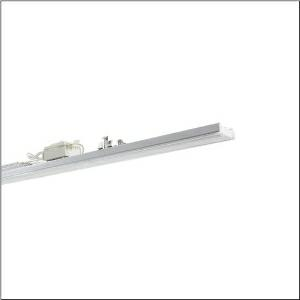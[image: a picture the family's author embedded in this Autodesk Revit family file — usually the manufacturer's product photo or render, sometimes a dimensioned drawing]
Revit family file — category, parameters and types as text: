
# Revit family: licross_r__11_recessed_mo_51tl1ecn49xg_c042
name_source: partatom
category: Lighting Fixtures
units: mm (PartAtom-declared; Revit-internal decimal feet)

## family parameters
Cut with Voids When Loaded = No
Host = Face
Light Source = No
Part Type = Normal
Room Calculation Point = No
Round Connector Dimension = Use Diameter
Shared = No

## types (1)
- --- (1 x LED, 9000 lm, 49.3 W, 4000K)
    Apparent Load = 49 VA
    CIE Flux Codes = 85 95 99 100 100
    Color Rendering = 80
    Color Temperature = 4000K
    Default Elevation = 1800 mm
    Description = Licross® 11 Recessed MO, luminaire insert, of sheet steel, coil coated, white, length: 1.500mm, width: 66mm, height: 67mm, LED rated luminous flux: 9.000lm, light colour: 840, control gear: ON/OFF Multilumen, CLOi, with plug, 3-pole, with phase selection, mains connection: 220..240V, AC, 50/60Hz, start of lifetime: 49W, end of service life: 55W, internal wiring halogen-free, primary light control with lens, of plastic, primary optical cover: cover, of PMMA, light emission: direct distribution, primary light characteristic: symmetric, protection rating (complete): IP40, insulation class (complete): insulation class I (protective earthing), certification: CE, ENEC, VDE, UKCA, protection symbol: D if used in an environment without relevant dust loads with corresponding accessories, impact resistance: IK06, permissible ambient temperature for indoor applications: -35..+40°C, corresponds to IFS (International Featured Standards) requirements for safety and quality in the food industry, reducing of maximum allowable ambient temperature of 5°C with ceiling mounting, LABS conformity tested according to VDMA 24364:2018-05, packaging unit: 1 piece
    Height = 58 mm
    Lamp = 1 x LED
    Lamp Light Flux = 9000 lm
    Lamp Power = 49.3 W
    Lamp count = 1
    Length = 1500 mm
    Luminous efficacy = 183 lm/W
    Manufacturer = Siteco
    ModVariant = No
    Model = 51TL1ECN49XG
    Mounting Place = Ceiling
    Mounting Type = Pendant
    Number of Poles = 1
    OnlyDefault = Yes
    Power Factor = 1
    Product Name = Licross® 11 Recessed MO
    Product group = luminaire insert | ceiling pendant
    ProductGroupID = 902
    Protection Class = Protection class I
    Protection Degree = IP 40
    RLX_Detail_Level = 1
    RLX_Emergency_Light_Flux = 0 lm
    RLX_Emergency_Type = 0
    RLX_Emergency_Type_DB = No
    RlxData = <blob elided: 22441 chars, md5=be4d740e>
    Socket = socket
    Standby Power = 0 W
    System Light Flux = 9000 lm
    System Power = 49 W
    Type Comments = factory setting: luminous flux: 100 % | (A | C | E) | 113 mA
    Type Image = l_1296930.jpg
    URL = http://relux.com
    VarID = @adj_105759
    Voltage = 0 V
    Weight = 0.00 kg
    Width = 66 mm

## geometry (parser evidence)
native form markers: Blend x4, Sweep x9
no freeform markers — native parametric forms only
